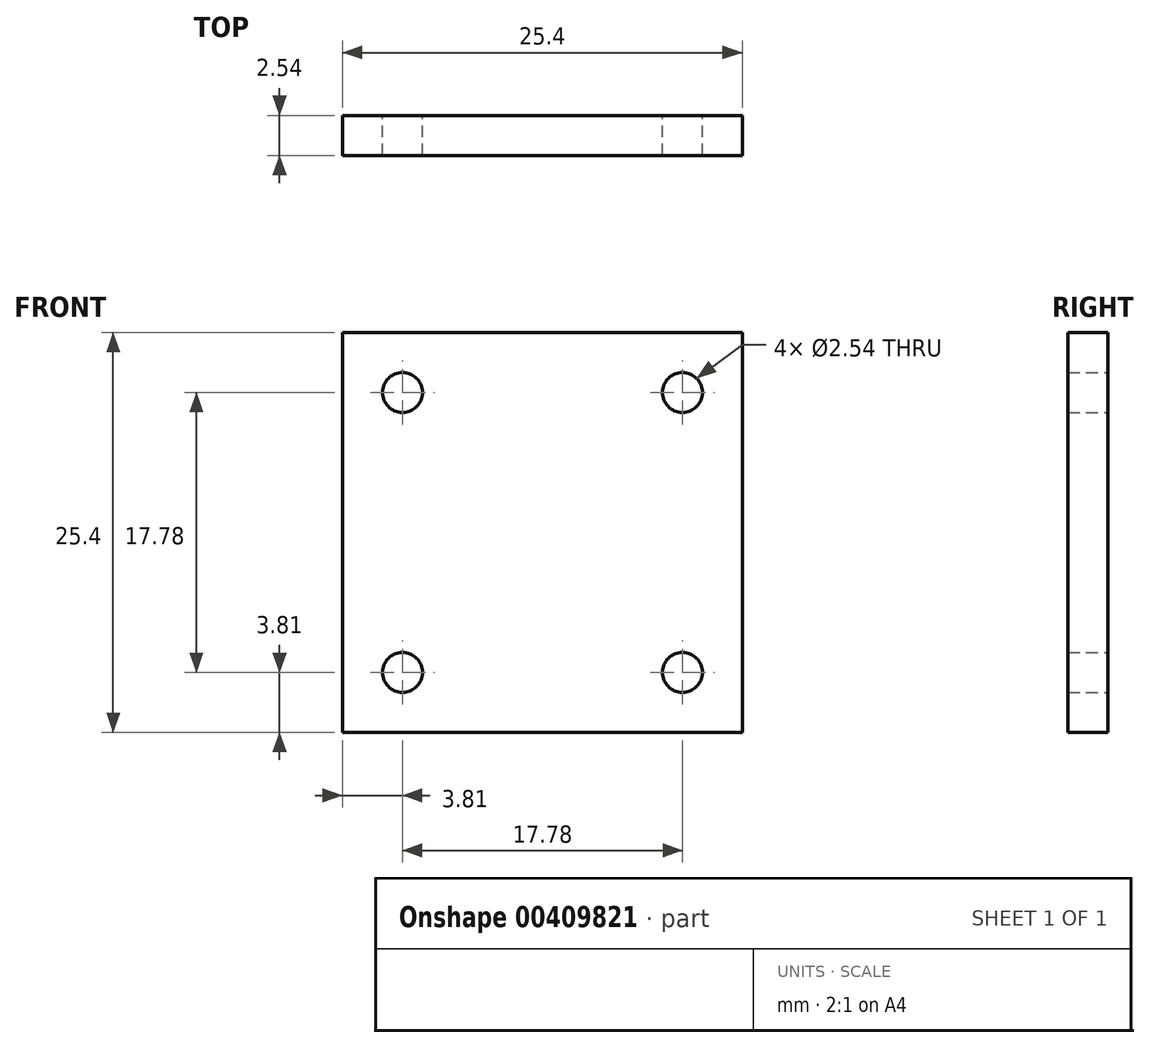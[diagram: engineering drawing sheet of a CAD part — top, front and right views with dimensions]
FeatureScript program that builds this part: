
annotation { "Feature Type Name" : "Feature", "Feature Type Description" : "" }
export const myFeature = defineFeature(function(context is Context, id is Id, definition is map)
    precondition{}
    {
        {
            var Q0;
            Q0=qCreatedBy(makeId("Front.planeOp"),FACE);
            var sketch = newSketch(context, id + "F0", { "sketchPlane" : qUnion([Q0])});
            skLineSegment(sketch, "E0.bottom", {"start": v(-12.7, 12.7) * mm, "end": v(12.7, 12.7) * mm});
            skLineSegment(sketch, "E0.top", {"start": v(-12.7, -12.7) * mm, "end": v(12.7, -12.7) * mm});
            skLineSegment(sketch, "E0.left", {"start": v(-12.7, 12.7) * mm, "end": v(-12.7, -12.7) * mm});
            skLineSegment(sketch, "E0.right", {"start": v(12.7, 12.7) * mm, "end": v(12.7, -12.7) * mm});
            skLineSegment(sketch, "E1", {"start": v(0, 0) * mm, "end": v(0, 38.1) * mm, "construction": true});
            skLineSegment(sketch, "E2", {"start": v(0, 0) * mm, "end": v(0, -32) * mm, "construction": true});
            skLineSegment(sketch, "E3", {"start": v(-30.04, 0) * mm, "end": v(35.12, 0) * mm, "construction": true});
            skCircle(sketch, "E4", {"center": v(-8.9, 8.89) * mm, "radius": 1.27 * mm});
            skLineSegment(sketch, "E5", {"start": v(-8.9, 8.89) * mm, "end": v(19.75, 8.89) * mm, "construction": true});
            skCircle(sketch, "E6.MirrorC", {"center": v(8.9, 8.89) * mm, "radius": 1.27 * mm});
            skCircle(sketch, "E7.MirrorC", {"center": v(8.9, -8.89) * mm, "radius": 1.27 * mm});
            skCircle(sketch, "E8.MirrorC", {"center": v(-8.9, -8.89) * mm, "radius": 1.27 * mm});
            skSolve(sketch);
        }
        {
            var Q0;
            Q0=makeQuery(id+"F0.imprint","IMPRINT",FACE,{"disambiguationData":[TD([[makeQuery(id+"F0.imprint","IMPRINT",EDGE,{"derivedFrom":sQuery(id+"F0.wireOp",EDGE,"E0.bottom")}),-1.0]])]});
            extrude(context, id + "F1", {"entities" : qUnion([Q0]), "depth" : 2.54 * mm});
        }
    });
